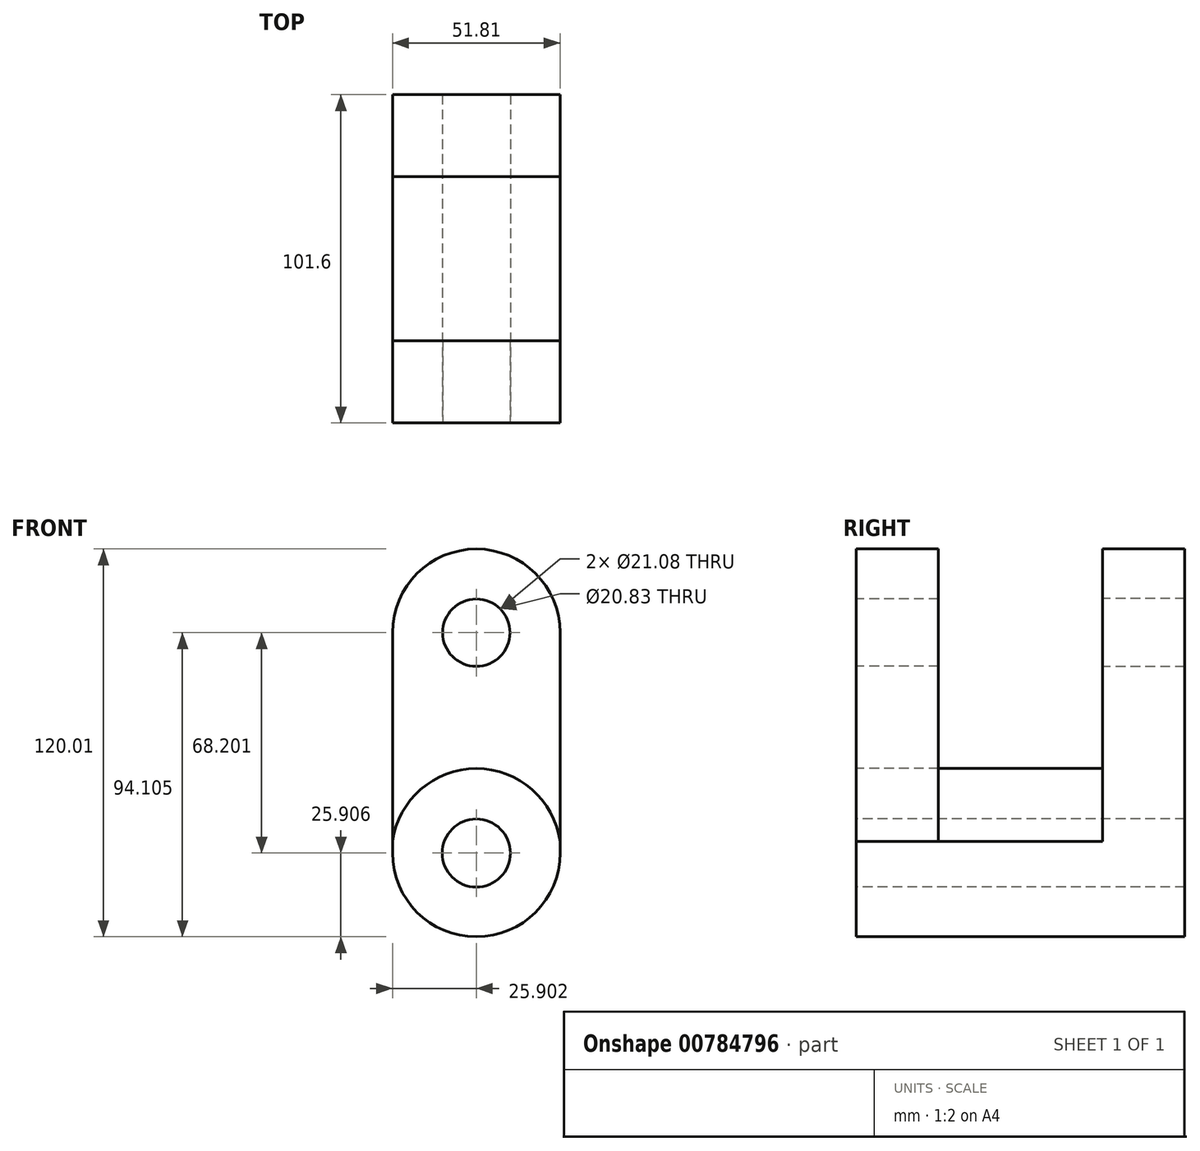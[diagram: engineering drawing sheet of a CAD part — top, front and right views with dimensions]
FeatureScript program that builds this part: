
annotation { "Feature Type Name" : "Feature", "Feature Type Description" : "" }
export const myFeature = defineFeature(function(context is Context, id is Id, definition is map)
    precondition{}
    {
        {
            var Q0;
            Q0=qCreatedBy(makeId("Front.planeOp"),FACE);
            var sketch = newSketch(context, id + "F0", { "sketchPlane" : qUnion([Q0])});
            skLineSegment(sketch, "E0", {"start": v(-39.88, 32.9) * mm, "end": v(-39.88, -17.95) * mm});
            skLineSegment(sketch, "E1", {"start": v(11.93, -17.95) * mm, "end": v(11.93, 50.25) * mm});
            skLineSegment(sketch, "E2", {"start": v(-39.88, 50.25) * mm, "end": v(-39.88, 32.9) * mm});
            skArc(sketch, "E3", {"start": v(11.93, 50.25) * mm, "mid": v(-13.98, 76.15) * mm, "end": v(-39.88, 50.25) * mm});
            skArc(sketch, "E4", {"start": v(-39.88, -17.95) * mm, "mid": v(-13.98, -43.86) * mm, "end": v(11.93, -17.95) * mm});
            skCircle(sketch, "E5", {"center": v(-13.98, 50.25) * mm, "radius": 10.54 * mm});
            skCircle(sketch, "E6", {"center": v(-13.98, -17.95) * mm, "radius": 10.54 * mm});
            skSolve(sketch);
        }
        {
            var Q0;
            Q0=makeQuery(id+"F0.imprint","IMPRINT",FACE,{"disambiguationData":[TD([[makeQuery(id+"F0.imprint","IMPRINT",EDGE,{"derivedFrom":sQuery(id+"F0.wireOp",EDGE,"E0")}),1.0]])]});
            extrude(context, id + "F1", {"entities" : qUnion([Q0]), "oppositeDirection" : true, "depth" : 25.4 * mm, "offsetDistance" : 25.4 * mm});
        }
        {
            var Q0;
            Q0=makeQuery(id+"F1.opExtrude","CAP_FACE",FACE,{"disambiguationData":[OSD([sQuery(id+"F0.wireOp",EDGE,"E0"),sQuery(id+"F0.wireOp",EDGE,"E1"),sQuery(id+"F0.wireOp",EDGE,"E2"),sQuery(id+"F0.wireOp",EDGE,"E3"),sQuery(id+"F0.wireOp",EDGE,"E4"),sQuery(id+"F0.wireOp",EDGE,"E5"),sQuery(id+"F0.wireOp",EDGE,"E6")])],"isStart":true});
            var sketch = newSketch(context, id + "F2", { "sketchPlane" : qUnion([Q0])});
            skCircle(sketch, "E7", {"center": v(-13.98, -17.95) * mm, "radius": 26.15 * mm});
            skSolve(sketch);
        }
        {
            var Q0;
            {var subQ0=makeQuery(id+"F1.opExtrude","CAP_EDGE",EDGE,{"disambiguationData":[OSD([sQuery(id+"F0.wireOp",EDGE,"E4")])],"isStart":true});Q0=makeQuery(id+"F2.imprint","IMPRINT",FACE,{"disambiguationData":[TD([[makeQuery(id+"F2.imprint","IMPRINT",EDGE,{"derivedFrom":subQ0}),1.0]])]});}
            extrude(context, id + "F3", {"entities" : qUnion([Q0]), "operationType" : NewBodyOperationType.ADD, "depth" : 76.2 * mm, "offsetDistance" : 25.4 * mm});
        }
        {
            var Q0;
            Q0=makeQuery(id+"F3.opExtrude","CAP_FACE",FACE,{"disambiguationData":[OSD([sQuery(id+"F0.wireOp",EDGE,"E0"),sQuery(id+"F0.wireOp",EDGE,"E1"),sQuery(id+"F0.wireOp",EDGE,"E2"),sQuery(id+"F0.wireOp",EDGE,"E4"),sQuery(id+"F0.wireOp",EDGE,"E6"),sQuery(id+"F2.wireOp",EDGE,"E7")])],"isStart":false});
            var sketch = newSketch(context, id + "F4", { "sketchPlane" : qUnion([Q0])});
            skLineSegment(sketch, "E8", {"start": v(11.93, -17.95) * mm, "end": v(11.93, 50.24) * mm});
            skLineSegment(sketch, "E9", {"start": v(-39.88, 50.24) * mm, "end": v(-39.88, -17.95) * mm});
            skArc(sketch, "E10", {"start": v(11.93, 50.24) * mm, "mid": v(-13.98, 76.15) * mm, "end": v(-39.88, 50.24) * mm});
            skArc(sketch, "E11", {"start": v(-39.88, -17.95) * mm, "mid": v(-12.06, -43.92) * mm, "end": v(11.93, -14.38) * mm});
            skCircle(sketch, "E12", {"center": v(-13.98, 50.24) * mm, "radius": 10.41 * mm});
            skSolve(sketch);
        }
        {
            var Q0;
            {var subQ0=sQuery(id+"F4.wireOp",EDGE,"E10");Q0=makeQuery(id+"F4.imprint","IMPRINT",FACE,{"disambiguationData":[TD([[makeQuery(id+"F4.imprint","IMPRINT",EDGE,{"derivedFrom":subQ0}),1.0]])]});}
            extrude(context, id + "F5", {"entities" : qUnion([Q0]), "oppositeDirection" : true, "depth" : 25.4 * mm, "offsetDistance" : 25.4 * mm});
        }
    });
